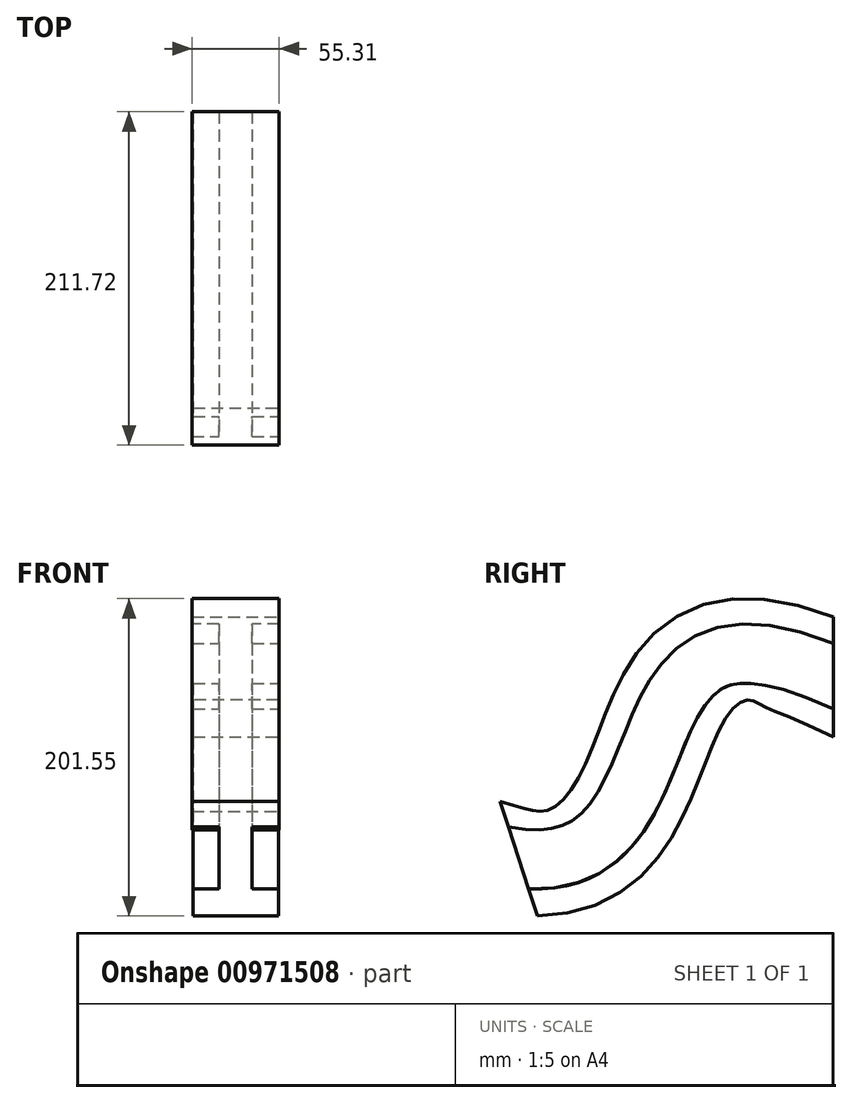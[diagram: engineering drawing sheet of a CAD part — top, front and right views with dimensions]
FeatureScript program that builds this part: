
annotation { "Feature Type Name" : "Feature", "Feature Type Description" : "" }
export const myFeature = defineFeature(function(context is Context, id is Id, definition is map)
    precondition{}
    {
        {
            var Q0;
            Q0=qCreatedBy(makeId("Front.planeOp"),FACE);
            var sketch = newSketch(context, id + "F0", { "sketchPlane" : qUnion([Q0])});
            skLineSegment(sketch, "E0.bottom", {"start": v(-27, 38.56) * mm, "end": v(28.3, 38.56) * mm});
            skLineSegment(sketch, "E0.top", {"start": v(-27, 21.6) * mm, "end": v(-9.85, 21.6) * mm});
            skLineSegment(sketch, "E0.left", {"start": v(-27, 38.56) * mm, "end": v(-27, 21.6) * mm});
            skLineSegment(sketch, "E0.right", {"start": v(28.3, 38.56) * mm, "end": v(28.3, 21.6) * mm});
            skLineSegment(sketch, "E1.bottom", {"start": v(-9.85, 38.56) * mm, "end": v(11.16, 38.56) * mm});
            skLineSegment(sketch, "E1.top", {"start": v(-9.85, -37.77) * mm, "end": v(11.16, -37.77) * mm});
            skLineSegment(sketch, "E1.left", {"start": v(-9.85, 21.6) * mm, "end": v(-9.85, -19.89) * mm});
            skLineSegment(sketch, "E1.right", {"start": v(11.16, 21.6) * mm, "end": v(11.16, -19.89) * mm});
            skLineSegment(sketch, "E2.bottom", {"start": v(-26.26, -19.89) * mm, "end": v(-9.85, -19.89) * mm});
            skLineSegment(sketch, "E2.top", {"start": v(-26.26, -37.77) * mm, "end": v(27.94, -37.77) * mm});
            skLineSegment(sketch, "E2.left", {"start": v(-26.26, -19.89) * mm, "end": v(-26.26, -37.77) * mm});
            skLineSegment(sketch, "E2.right", {"start": v(27.94, -19.89) * mm, "end": v(27.94, -37.77) * mm});
            skLineSegment(sketch, "E3.trimOffspring", {"start": v(11.16, 21.6) * mm, "end": v(28.3, 21.6) * mm});
            skLineSegment(sketch, "E4.trimOffspring", {"start": v(11.16, -19.89) * mm, "end": v(27.94, -19.89) * mm});
            skSolve(sketch);
        }
        {
            var Q0;
            Q0=qCreatedBy(makeId("Right.planeOp"),FACE);
            var sketch = newSketch(context, id + "F1", { "sketchPlane" : qUnion([Q0])});
            skFitSpline(sketch, "E5", {"points": [v(0, 0) * mm, v(-113.38, -40.83) * mm, v(-199.76, -115.44) * mm], "startDerivative": vector(-471.32, 203.94) * mm, "endDerivative": vector(-341.18, 31.84) * mm});
            skSolve(sketch);
        }
        {
            var Q0;
            Q0=makeQuery(id+"F0.imprint","IMPRINT",FACE,{"disambiguationData":[TD([[makeQuery(id+"F0.imprint","IMPRINT",EDGE,{"derivedFrom":sQuery(id+"F0.wireOp",EDGE,"E0.top")}),1.0]])]});
            var Q1;
            Q1=sQuery(id+"F1.wireOp",EDGE,"E5");
            sweep(context, id + "F2", {"profiles" : qUnion([Q0]), "path" : qUnion([Q1])});
        }
    });
